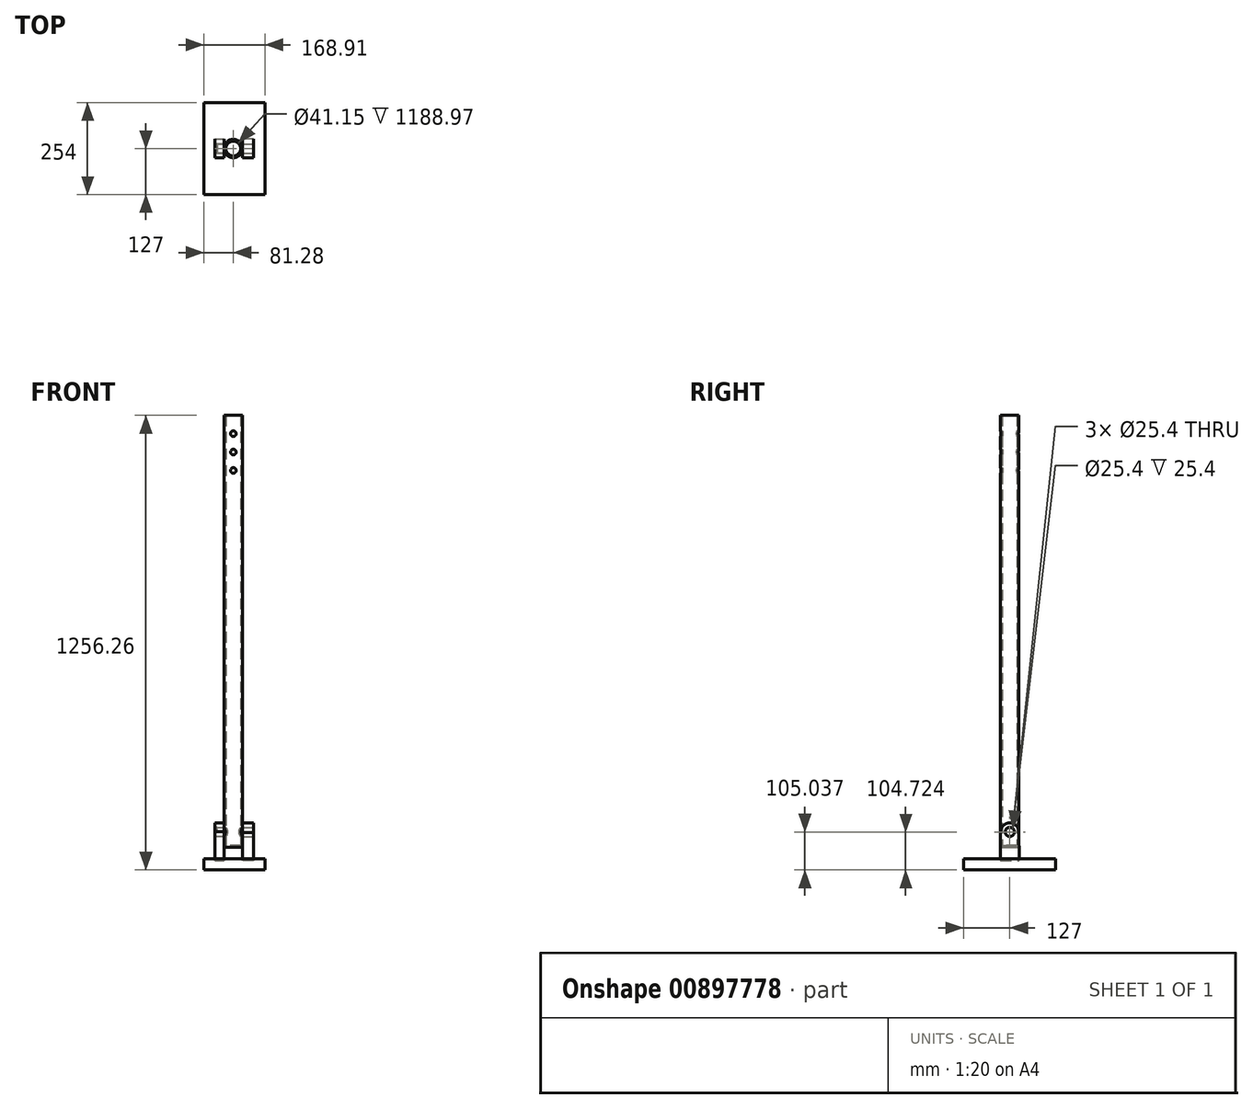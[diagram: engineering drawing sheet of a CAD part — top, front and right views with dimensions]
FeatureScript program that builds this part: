
annotation { "Feature Type Name" : "Feature", "Feature Type Description" : "" }
export const myFeature = defineFeature(function(context is Context, id is Id, definition is map)
    precondition{}
    {
        {
            var Q0;
            Q0=qCreatedBy(makeId("Top.planeOp"),FACE);
            var sketch = newSketch(context, id + "F0", { "sketchPlane" : qUnion([Q0])});
            skCircle(sketch, "E0", {"center": v(0, 0) * mm, "radius": 25.4 * mm});
            skSolve(sketch);
        }
        {
            var Q0;
            Q0=makeQuery(id+"F0.imprint","IMPRINT",FACE,{"disambiguationData":[TD([[makeQuery(id+"F0.imprint","IMPRINT",EDGE,{"derivedFrom":sQuery(id+"F0.wireOp",EDGE,"E0")}),1.0]])]});
            extrude(context, id + "F1", {"entities" : qUnion([Q0]), "depth" : 1193.8 * mm, "offsetDistance" : 25.4 * mm});
        }
        {
            var Q0;
            Q0=makeQuery(id+"F1.opExtrude","CAP_FACE",FACE,{"disambiguationData":[OSD([sQuery(id+"F0.wireOp",EDGE,"E0")])],"isStart":false});
            shell(context, id + "F2", {"entities" : qUnion([Q0]), "thickness" : 4.83 * mm});
        }
        {
            var Q0;
            Q0=qCreatedBy(makeId("Front.planeOp"),FACE);
            var sketch = newSketch(context, id + "F3", { "sketchPlane" : qUnion([Q0])});
            skCircle(sketch, "E1", {"center": v(0, 1143) * mm, "radius": 7.62 * mm});
            skCircle(sketch, "E2.0.1.0", {"center": v(0, 1092.2) * mm, "radius": 7.62 * mm});
            skCircle(sketch, "E2.0.2.0", {"center": v(0, 1041.4) * mm, "radius": 7.62 * mm});
            skCircle(sketch, "E2.1.0.0", {"center": v(0.25, 1143) * mm, "radius": 7.62 * mm});
            skCircle(sketch, "E2.1.1.0", {"center": v(0.25, 1092.2) * mm, "radius": 7.62 * mm});
            skCircle(sketch, "E2.1.2.0", {"center": v(0.25, 1041.4) * mm, "radius": 7.62 * mm});
            skLineSegment(sketch, "E2.direction1", {"start": v(0, 1143) * mm, "end": v(0.25, 1143) * mm, "construction": true});
            skLineSegment(sketch, "E2.direction2", {"start": v(0, 1143) * mm, "end": v(0, 1092.2) * mm, "construction": true});
            skSolve(sketch);
        }
        {
            var Q0;
            Q0 = qSketchRegion(id + "F3", true);
            extrude(context, id + "F4", {"entities" : qUnion([Q0]), "operationType" : NewBodyOperationType.REMOVE, "endBound" : BoundingType.THROUGH_ALL, "oppositeDirection" : true, "depth" : 25.4 * mm, "offsetDistance" : 25.4 * mm, "hasSecondDirection" : true, "secondDirectionOppositeDirection" : false, "secondDirectionDepth" : 25.4 * mm});
        }
        {
            var Q0;
            Q0=qCreatedBy(makeId("Right.planeOp"),FACE);
            cPlane(context, id + "F5", {"entities" : qUnion([Q0]), "cplaneType" : CPlaneType.OFFSET, "offset" : 25.4 * mm, "width" : 152.4 * mm, "height" : 152.4 * mm});
        }
        {
            var Q0;
            Q0=qCreatedBy(id+"F5.planeOp",FACE);
            var sketch = newSketch(context, id + "F6", { "sketchPlane" : qUnion([Q0])});
            skLineSegment(sketch, "E3", {"start": v(-25.4, -31.18) * mm, "end": v(-127, -31.18) * mm});
            skLineSegment(sketch, "E4", {"start": v(-127, -31.18) * mm, "end": v(-127, -62.46) * mm});
            skLineSegment(sketch, "E5", {"start": v(25.4, -31.18) * mm, "end": v(127, -31.18) * mm});
            skLineSegment(sketch, "E6", {"start": v(-127, -62.46) * mm, "end": v(127, -62.46) * mm});
            skLineSegment(sketch, "E7", {"start": v(127, -31.18) * mm, "end": v(127, -62.46) * mm});
            skLineSegment(sketch, "E8", {"start": v(-25.4, -31.18) * mm, "end": v(25.4, -31.18) * mm});
            skSolve(sketch);
        }
        {
            var Q0;
            Q0=qCreatedBy(id+"F5.planeOp",FACE);
            var sketch = newSketch(context, id + "F7", { "sketchPlane" : qUnion([Q0])});
            skArc(sketch, "E9", {"start": v(25.4, 42.58) * mm, "mid": v(-0.72, 67.65) * mm, "end": v(-25.37, 41.13) * mm});
            skLineSegment(sketch, "E10", {"start": v(-25.37, 43.4) * mm, "end": v(-25.37, -36.13) * mm});
            skLineSegment(sketch, "E11", {"start": v(26.37, -36.13) * mm, "end": v(25.4, 42.58) * mm});
            skLineSegment(sketch, "E12", {"start": v(-25.37, -36.13) * mm, "end": v(26.37, -36.13) * mm});
            skSolve(sketch);
        }
        {
            var Q0;
            Q0 = qSketchRegion(id + "F6", true);
            extrude(context, id + "F8", {"entities" : qUnion([Q0]), "depth" : 62.23 * mm, "offsetDistance" : 25.4 * mm, "hasSecondDirection" : true, "secondDirectionOppositeDirection" : true, "secondDirectionDepth" : 106.68 * mm});
        }
        {
            var Q0;
            Q0 = qSketchRegion(id + "F7", true);
            var Q1;
            Q1=makeQuery(id+"F8.opExtrude","CAP_FACE",FACE,{"disambiguationData":[OSD([sQuery(id+"F6.wireOp",EDGE,"E3"),sQuery(id+"F6.wireOp",EDGE,"E4"),sQuery(id+"F6.wireOp",EDGE,"E5"),sQuery(id+"F6.wireOp",EDGE,"E6"),sQuery(id+"F6.wireOp",EDGE,"E7"),sQuery(id+"F6.wireOp",EDGE,"E8")])],"isStart":false});
            extrude(context, id + "F9", {"entities" : qUnion([Q0]), "depth" : 30.99 * mm, "endBoundEntityFace" : qUnion([Q1]), "offsetDistance" : 25.4 * mm});
        }
        {
            var Q0;
            Q0=qCreatedBy(makeId("Right.planeOp"),FACE);
            cPlane(context, id + "F10", {"entities" : qUnion([Q0]), "cplaneType" : CPlaneType.OFFSET, "offset" : 25.4 * mm, "oppositeDirection" : true, "width" : 152.4 * mm, "height" : 152.4 * mm});
        }
        {
            var Q0;
            Q0=qCreatedBy(id+"F10.planeOp",FACE);
            var sketch = newSketch(context, id + "F11", { "sketchPlane" : qUnion([Q0])});
            skArc(sketch, "E13.0", {"start": v(25.4, 42.58) * mm, "mid": v(-0.72, 67.65) * mm, "end": v(-25.37, 41.13) * mm});
            skLineSegment(sketch, "E14.0", {"start": v(-25.37, 43.4) * mm, "end": v(-25.37, -36.13) * mm});
            skLineSegment(sketch, "E15.0", {"start": v(26.37, -36.13) * mm, "end": v(25.4, 42.58) * mm});
            skLineSegment(sketch, "E16", {"start": v(26.37, -36.13) * mm, "end": v(-25.37, -36.13) * mm});
            skSolve(sketch);
        }
        {
            var Q0;
            {var subQ0=sQuery(id+"F11.wireOp",EDGE,"E15.0");Q0=makeQuery(id+"F11.imprint","IMPRINT",FACE,{"disambiguationData":[TD([[makeQuery(id+"F11.imprint","IMPRINT",EDGE,{"derivedFrom":subQ0}),1.0]])]});}
            var Q1;
            Q1=makeQuery(id+"F8.opExtrude","CAP_FACE",FACE,{"disambiguationData":[OSD([sQuery(id+"F6.wireOp",EDGE,"E3"),sQuery(id+"F6.wireOp",EDGE,"E4"),sQuery(id+"F6.wireOp",EDGE,"E5"),sQuery(id+"F6.wireOp",EDGE,"E6"),sQuery(id+"F6.wireOp",EDGE,"E7"),sQuery(id+"F6.wireOp",EDGE,"E8")])],"isStart":true});
            extrude(context, id + "F12", {"entities" : qUnion([Q0]), "oppositeDirection" : true, "depth" : 25.4 * mm, "endBoundEntityFace" : qUnion([Q1]), "offsetDistance" : 25.4 * mm});
        }
        {
            var Q0;
            Q0=makeQuery(id+"F9.opExtrude","CAP_FACE",FACE,{"disambiguationData":[OSD([sQuery(id+"F7.wireOp",EDGE,"E9"),sQuery(id+"F7.wireOp",EDGE,"E10"),sQuery(id+"F7.wireOp",EDGE,"E11"),sQuery(id+"F7.wireOp",EDGE,"E12")])],"isStart":false});
            var sketch = newSketch(context, id + "F13", { "sketchPlane" : qUnion([Q0])});
            skCircle(sketch, "E17", {"center": v(0, 42.58) * mm, "radius": 12.7 * mm});
            skSolve(sketch);
        }
        {
            var Q0;
            Q0=makeQuery(id+"F13.imprint","IMPRINT",FACE,{"disambiguationData":[TD([[makeQuery(id+"F13.imprint","IMPRINT",EDGE,{"derivedFrom":sQuery(id+"F13.wireOp",EDGE,"E17")}),1.0]])]});
            extrude(context, id + "F14", {"entities" : qUnion([Q0]), "operationType" : NewBodyOperationType.REMOVE, "oppositeDirection" : true, "depth" : 100.58 * mm, "offsetDistance" : 25.4 * mm});
        }
        {
            var Q0;
            Q0=makeQuery(id+"F12.opExtrude","CAP_FACE",FACE,{"disambiguationData":[OSD([sQuery(id+"F11.wireOp",EDGE,"E13.0"),sQuery(id+"F11.wireOp",EDGE,"E14.0"),sQuery(id+"F11.wireOp",EDGE,"E15.0"),sQuery(id+"F11.wireOp",EDGE,"E16")])],"isStart":false});
            var sketch = newSketch(context, id + "F15", { "sketchPlane" : qUnion([Q0])});
            skCircle(sketch, "E18", {"center": v(0, 42.26) * mm, "radius": 12.7 * mm});
            skSolve(sketch);
        }
        {
            var Q0;
            Q0=makeQuery(id+"F15.imprint","IMPRINT",FACE,{"disambiguationData":[TD([[makeQuery(id+"F15.imprint","IMPRINT",EDGE,{"derivedFrom":sQuery(id+"F15.wireOp",EDGE,"E18")}),1.0]])]});
            extrude(context, id + "F16", {"entities" : qUnion([Q0]), "operationType" : NewBodyOperationType.REMOVE, "oppositeDirection" : true, "depth" : 25.4 * mm, "offsetDistance" : 25.4 * mm});
        }
    });
